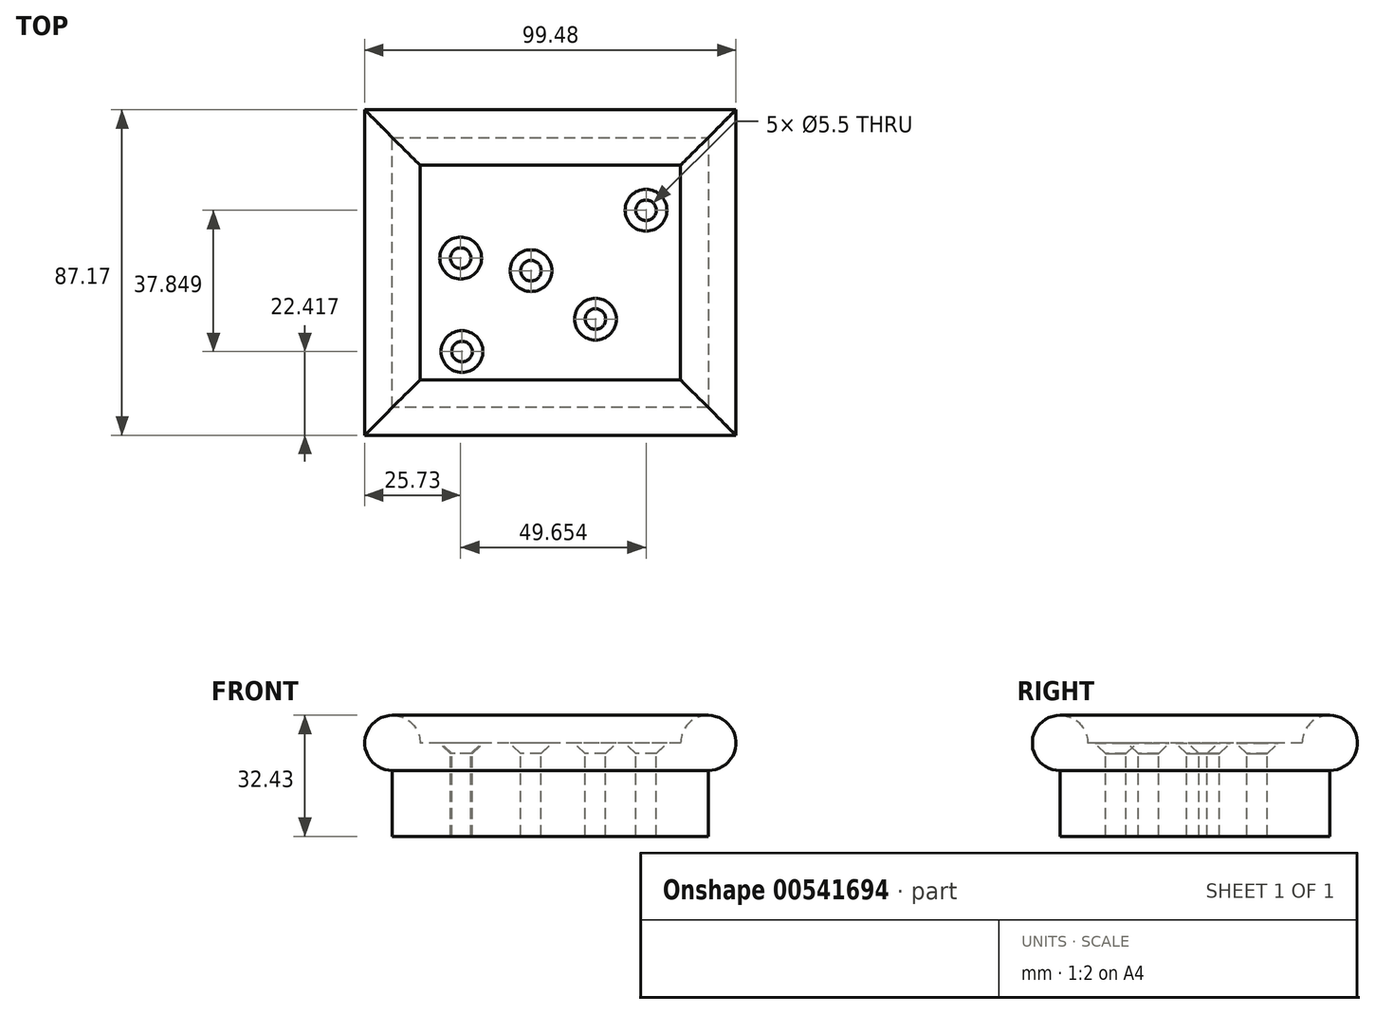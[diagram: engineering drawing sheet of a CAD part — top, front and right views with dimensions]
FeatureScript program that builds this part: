
annotation { "Feature Type Name" : "Feature", "Feature Type Description" : "" }
export const myFeature = defineFeature(function(context is Context, id is Id, definition is map)
    precondition{}
    {
        {
            var Q0;
            Q0=qCreatedBy(makeId("Top.planeOp"),FACE);
            var sketch = newSketch(context, id + "F0", { "sketchPlane" : qUnion([Q0])});
            skLineSegment(sketch, "E0.bottom", {"start": v(-37.13, 35.65) * mm, "end": v(47.5, 35.65) * mm});
            skLineSegment(sketch, "E0.top", {"start": v(-37.13, -36.66) * mm, "end": v(47.5, -36.66) * mm});
            skLineSegment(sketch, "E0.left", {"start": v(-37.13, 35.65) * mm, "end": v(-37.13, -36.66) * mm});
            skLineSegment(sketch, "E0.right", {"start": v(47.5, 35.65) * mm, "end": v(47.5, -36.66) * mm});
            skSolve(sketch);
        }
        {
            var Q0;
            Q0 = qSketchRegion(id + "F0", true);
            extrude(context, id + "F1", {"entities" : qUnion([Q0]), "depth" : 25 * mm, "offsetDistance" : 25 * mm});
        }
        {
            var Q0;
            Q0=makeQuery(id+"F1.opExtrude","CAP_FACE",FACE,{"disambiguationData":[OSD([sQuery(id+"F0.wireOp",EDGE,"E0.bottom"),sQuery(id+"F0.wireOp",EDGE,"E0.top"),sQuery(id+"F0.wireOp",EDGE,"E0.left"),sQuery(id+"F0.wireOp",EDGE,"E0.right")])],"isStart":false});
            var sketch = newSketch(context, id + "F2", { "sketchPlane" : qUnion([Q0])});
            skPoint(sketch, "E1", {"position": v(-18.47, -21.67) * mm});
            skPoint(sketch, "E2", {"position": v(-18.83, 3.37) * mm});
            skPoint(sketch, "E3", {"position": v(17.27, -12.97) * mm});
            skPoint(sketch, "E4", {"position": v(30.82, 16.18) * mm});
            skPoint(sketch, "E5", {"position": v(0, 0) * mm});
            skSolve(sketch);
        }
        {
            var Q0;
            Q0=sQuery(id+"F2.wireOp",VERTEX,"E1");
            var Q1;
            Q1=sQuery(id+"F2.wireOp",VERTEX,"E3");
            var Q2;
            Q2=sQuery(id+"F2.wireOp",VERTEX,"E5");
            var Q3;
            Q3=sQuery(id+"F2.wireOp",VERTEX,"E2");
            var Q4;
            Q4=sQuery(id+"F2.wireOp",VERTEX,"E4");
            var Q5;
            Q5=makeQuery(id+"F1.opExtrude","SWEPT_BODY",BODY,{"disambiguationData":[OSD([sQuery(id+"F0.wireOp",EDGE,"E0.bottom"),sQuery(id+"F0.wireOp",EDGE,"E0.top"),sQuery(id+"F0.wireOp",EDGE,"E0.left"),sQuery(id+"F0.wireOp",EDGE,"E0.right")])]});
            hole(context, id + "F3", {"style" : HoleStyle.C_SINK, "endStyle" : HoleEndStyle.THROUGH, "standardTappedOrClearance" : lookupTablePath({ "standard" : "ISO", "fit" : "Normal", "size" : "M5", "type" : "Clearance" }), "standardBlindInLast" : lookupTablePath({ "fit" : "Standard", "standard" : "ISO", "size" : "M5", "type" : "Clearance" }), "holeDiameter" : 5.5 * mm, "cSinkDiameter" : 11.2 * mm, "cSinkAngle" : 90 * degree, "isTappedThrough" : true, "tappedDepth" : 12 * mm, "tapClearance" : 3, "startFromSketch" : true, "locations" : qUnion([Q0, Q1, Q2, Q3, Q4]), "scope" : qUnion([Q5])});
        }
        {
            var Q0;
            Q0=makeQuery(id+"F1.opExtrude","SWEPT_FACE",FACE,{"disambiguationData":[OSD([sQuery(id+"F0.wireOp",EDGE,"E0.left")])]});
            var sketch = newSketch(context, id + "F4", { "sketchPlane" : qUnion([Q0])});
            skCircle(sketch, "E6", {"center": v(-35.65, 25) * mm, "radius": 7.43 * mm});
            skSolve(sketch);
        }
        {
            var Q0;
            {var subQ0=sQuery(id+"F4.wireOp",EDGE,"E6");var subQ1=sQuery(id+"F0.wireOp",EDGE,"E0.left");var subQ4=makeQuery(id+"F1.opExtrude","CAP_EDGE",EDGE,{"disambiguationData":[OSD([subQ1])],"isStart":false});var subQ5=makeQuery(id+"F4.imprint","INTERSECT",VERTEX,{"derivedFrom":[subQ4,subQ0]});Q0=makeQuery(id+"F4.imprint","IMPRINT",FACE,{"disambiguationData":[TD([[makeQuery(id+"F4.imprint","IMPRINT",EDGE,{"disambiguationData":[TD([[subQ5,-1.0]])],"derivedFrom":subQ0}),1.0]])]});}
            var Q1;
            Q1=makeQuery(id+"F1.opExtrude","CAP_EDGE",EDGE,{"disambiguationData":[OSD([sQuery(id+"F0.wireOp",EDGE,"E0.bottom")])],"isStart":false});
            var Q2;
            Q2=makeQuery(id+"F1.opExtrude","CAP_EDGE",EDGE,{"disambiguationData":[OSD([sQuery(id+"F0.wireOp",EDGE,"E0.right")])],"isStart":false});
            var Q3;
            Q3=makeQuery(id+"F1.opExtrude","CAP_EDGE",EDGE,{"disambiguationData":[OSD([sQuery(id+"F0.wireOp",EDGE,"E0.top")])],"isStart":false});
            var Q4;
            Q4=makeQuery(id+"F1.opExtrude","CAP_EDGE",EDGE,{"disambiguationData":[OSD([sQuery(id+"F0.wireOp",EDGE,"E0.left")])],"isStart":false});
            sweep(context, id + "F5", {"operationType" : NewBodyOperationType.ADD, "profiles" : qUnion([Q0]), "path" : qUnion([Q1, Q2, Q3, Q4])});
        }
    });
